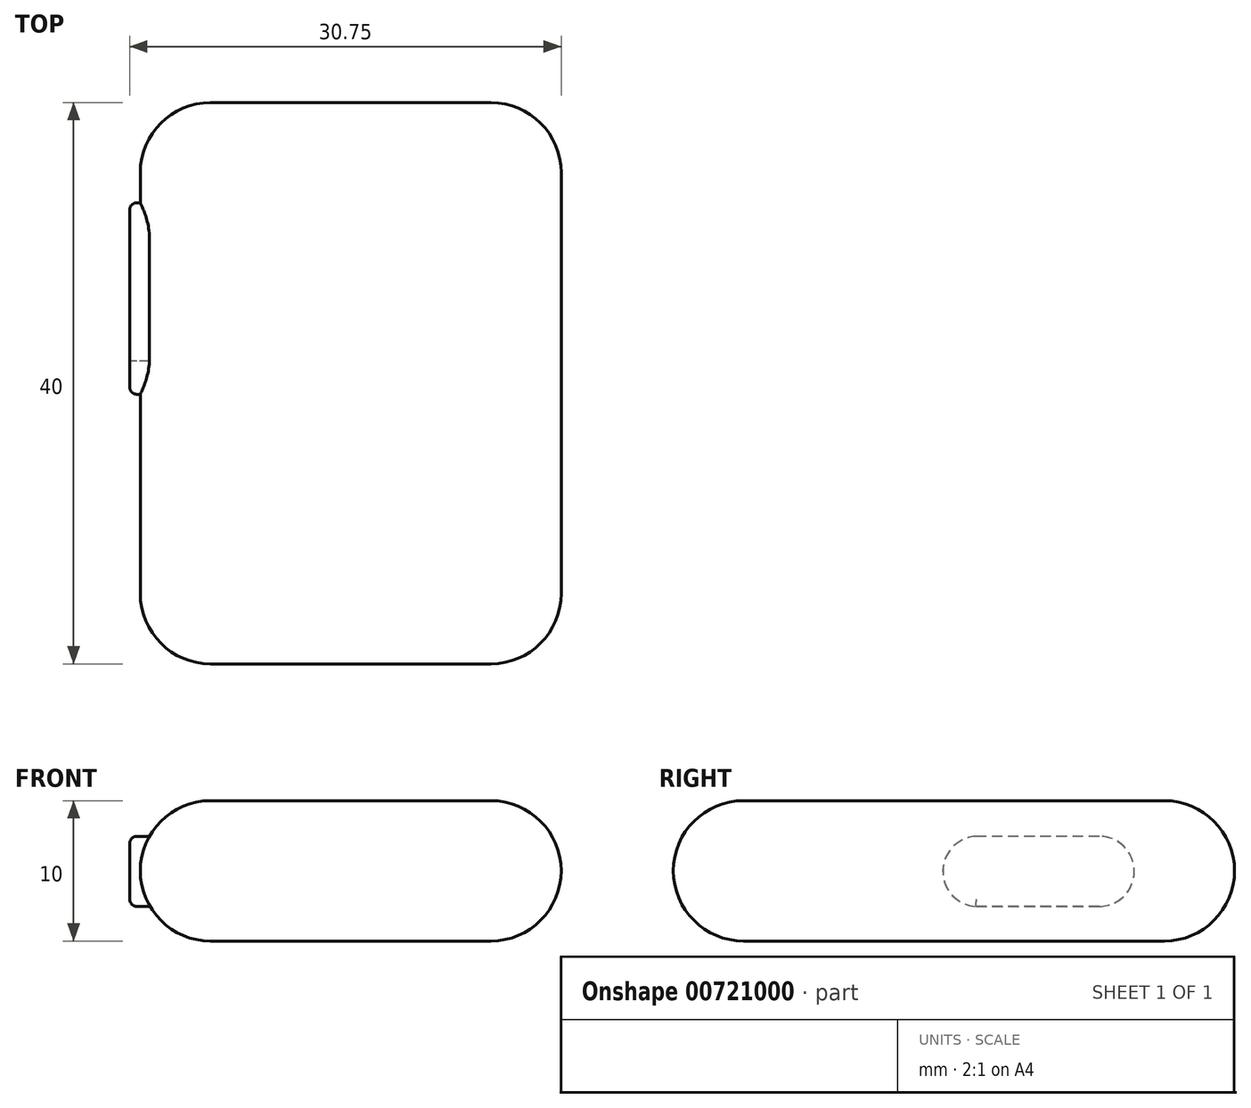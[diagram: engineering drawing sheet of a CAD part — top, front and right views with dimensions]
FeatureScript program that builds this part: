
annotation { "Feature Type Name" : "Feature", "Feature Type Description" : "" }
export const myFeature = defineFeature(function(context is Context, id is Id, definition is map)
    precondition{}
    {
        {
            var Q0;
            Q0=qCreatedBy(makeId("Top.planeOp"),FACE);
            var sketch = newSketch(context, id + "F0", { "sketchPlane" : qUnion([Q0])});
            skLineSegment(sketch, "E0.bottom", {"start": v(15, 20) * mm, "end": v(-15, 20) * mm});
            skLineSegment(sketch, "E0.top", {"start": v(15, -20) * mm, "end": v(-15, -20) * mm});
            skLineSegment(sketch, "E0.left", {"start": v(15, 20) * mm, "end": v(15, -20) * mm});
            skLineSegment(sketch, "E0.right", {"start": v(-15, 20) * mm, "end": v(-15, -20) * mm});
            skPoint(sketch, "E0.middle", {"position": v(0, 0) * mm});
            skSolve(sketch);
        }
        {
            var Q0;
            Q0=makeQuery(id+"F0.imprint","IMPRINT",FACE,{"disambiguationData":[TD([[makeQuery(id+"F0.imprint","IMPRINT",EDGE,{"derivedFrom":sQuery(id+"F0.wireOp",EDGE,"E0.bottom")}),1.0]])]});
            extrude(context, id + "F1", {"entities" : qUnion([Q0]), "oppositeDirection" : true, "depth" : 10 * mm, "offsetDistance" : 25.4 * mm});
        }
        {
            var Q0;
            Q0=makeQuery(id+"F1.opExtrude","SWEPT_EDGE",EDGE,{"disambiguationData":[OSD([sQuery(id+"F0.wireOp",EDGE,"E0.bottom"),sQuery(id+"F0.wireOp",EDGE,"E0.left")])]});
            var Q1;
            Q1=makeQuery(id+"F1.opExtrude","SWEPT_EDGE",EDGE,{"disambiguationData":[OSD([sQuery(id+"F0.wireOp",EDGE,"E0.bottom"),sQuery(id+"F0.wireOp",EDGE,"E0.right")])]});
            var Q2;
            Q2=makeQuery(id+"F1.opExtrude","SWEPT_EDGE",EDGE,{"disambiguationData":[OSD([sQuery(id+"F0.wireOp",EDGE,"E0.top"),sQuery(id+"F0.wireOp",EDGE,"E0.left")])]});
            var Q3;
            Q3=makeQuery(id+"F1.opExtrude","SWEPT_EDGE",EDGE,{"disambiguationData":[OSD([sQuery(id+"F0.wireOp",EDGE,"E0.top"),sQuery(id+"F0.wireOp",EDGE,"E0.right")])]});
            fillet(context, id + "F2", {"entities" : qUnion([Q0, Q1, Q2, Q3]), "radius" : 5 * mm, "tangentPropagation" : true, "allowEdgeOverflow" : false});
        }
        {
            var Q0;
            Q0=makeQuery(id+"F1.opExtrude","CAP_EDGE",EDGE,{"disambiguationData":[OSD([sQuery(id+"F0.wireOp",EDGE,"E0.left")])],"isStart":true});
            var Q1;
            Q1=makeQuery(id+"F1.opExtrude","CAP_EDGE",EDGE,{"disambiguationData":[OSD([sQuery(id+"F0.wireOp",EDGE,"E0.left")])],"isStart":false});
            fillet(context, id + "F3", {"entities" : qUnion([Q0, Q1]), "radius" : 5 * mm, "tangentPropagation" : true, "allowEdgeOverflow" : false});
        }
        {
            var Q0;
            Q0=qCreatedBy(makeId("Right.planeOp"),FACE);
            cPlane(context, id + "F4", {"entities" : qUnion([Q0]), "cplaneType" : CPlaneType.OFFSET, "offset" : 15 * mm, "oppositeDirection" : true, "width" : 152.4 * mm, "height" : 152.4 * mm});
        }
        {
            var Q0;
            Q0=qCreatedBy(id+"F4.planeOp",FACE);
            var sketch = newSketch(context, id + "F5", { "sketchPlane" : qUnion([Q0])});
            skCircle(sketch, "E1", {"center": v(10.35, -5.04) * mm, "radius": 2.5 * mm});
            skCircle(sketch, "E2", {"center": v(1.7, -5.04) * mm, "radius": 2.5 * mm});
            skLineSegment(sketch, "E3", {"start": v(10.35, -2.54) * mm, "end": v(1.7, -2.54) * mm});
            skLineSegment(sketch, "E4", {"start": v(1.58, -7.53) * mm, "end": v(10.35, -7.54) * mm});
            skSolve(sketch);
        }
        {
            var Q0;
            {var subQ0=sQuery(id+"F5.wireOp",EDGE,"E1");var subQ1=makeQuery(id+"F5.imprint","INTERSECT",VERTEX,{"derivedFrom":[subQ0,sQuery(id+"F5.wireOp",EDGE,"E3")]});Q0=makeQuery(id+"F5.imprint","IMPRINT",FACE,{"disambiguationData":[TD([[makeQuery(id+"F5.imprint","IMPRINT",EDGE,{"disambiguationData":[TD([[subQ1,-1.0]])],"derivedFrom":subQ0}),1.0]])]});}
            var Q1;
            {var subQ0=sQuery(id+"F5.wireOp",EDGE,"E4");var subQ1=sQuery(id+"F5.wireOp",EDGE,"E2");var subQ2=makeQuery(id+"F5.imprint","INTERSECT",VERTEX,{"disambiguationData":[OD(0.0)],"derivedFrom":[subQ1,subQ0]});Q1=makeQuery(id+"F5.imprint","IMPRINT",FACE,{"disambiguationData":[TD([[makeQuery(id+"F5.imprint","IMPRINT",EDGE,{"disambiguationData":[TD([[subQ2,-1.0]])],"derivedFrom":subQ1}),1.0]])]});}
            var Q2;
            {var subQ0=sQuery(id+"F5.wireOp",EDGE,"E3");Q2=makeQuery(id+"F5.imprint","IMPRINT",FACE,{"disambiguationData":[TD([[makeQuery(id+"F5.imprint","IMPRINT",EDGE,{"derivedFrom":subQ0}),1.0]])]});}
            var Q3;
            {var subQ0=sQuery(id+"F5.wireOp",EDGE,"E2");var subQ1=makeQuery(id+"F5.imprint","INTERSECT",VERTEX,{"derivedFrom":[subQ0,sQuery(id+"F5.wireOp",EDGE,"E3")]});Q3=makeQuery(id+"F5.imprint","IMPRINT",FACE,{"disambiguationData":[TD([[makeQuery(id+"F5.imprint","IMPRINT",EDGE,{"disambiguationData":[TD([[subQ1,-1.0]])],"derivedFrom":subQ0}),1.0]])]});}
            extrude(context, id + "F6", {"entities" : qUnion([Q0, Q1, Q2, Q3]), "operationType" : NewBodyOperationType.ADD, "endBound" : BoundingType.SYMMETRIC, "depth" : 1.5 * mm, "offsetDistance" : 25.4 * mm});
        }
        {
            var Q0;
            Q0=makeQuery(id+"F6.opExtrude","CAP_EDGE",EDGE,{"disambiguationData":[OSD([sQuery(id+"F5.wireOp",EDGE,"E4")])],"isStart":true});
            var Q1;
            Q1=makeQuery(id+"F6.opExtrude","CAP_EDGE",EDGE,{"disambiguationData":[OSD([sQuery(id+"F5.wireOp",EDGE,"E2")])],"isStart":true});
            var Q2;
            Q2=makeQuery(id+"F6.opExtrude","CAP_EDGE",EDGE,{"disambiguationData":[OSD([sQuery(id+"F5.wireOp",EDGE,"E1")])],"isStart":true});
            fillet(context, id + "F7", {"entities" : qUnion([Q0, Q1, Q2]), "radius" : 0.5 * mm, "tangentPropagation" : true, "allowEdgeOverflow" : false});
        }
    });
